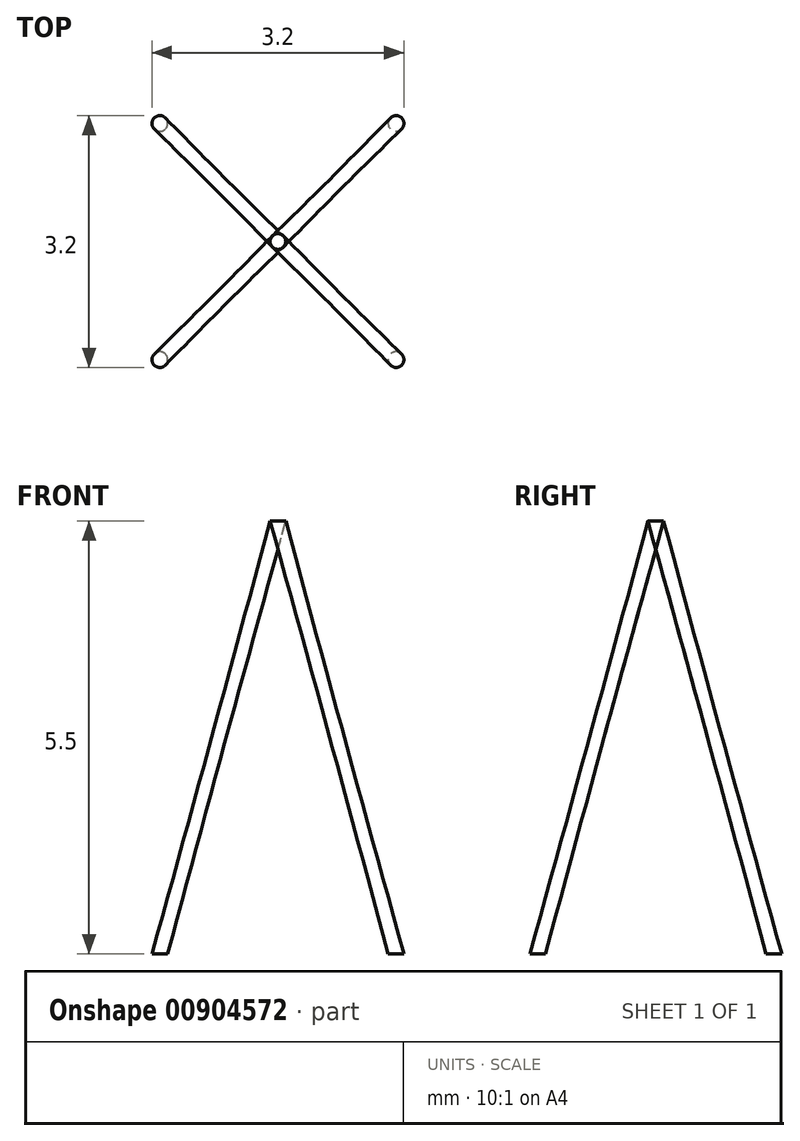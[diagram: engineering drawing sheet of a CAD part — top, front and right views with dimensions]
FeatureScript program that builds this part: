
annotation { "Feature Type Name" : "Feature", "Feature Type Description" : "" }
export const myFeature = defineFeature(function(context is Context, id is Id, definition is map)
    precondition{}
    {
        {
            var Q0;
            Q0=qCreatedBy(makeId("Top.planeOp"),FACE);
            var sketch = newSketch(context, id + "F0", { "sketchPlane" : qUnion([Q0])});
            skCircle(sketch, "E0", {"center": v(0, 0) * mm, "radius": 5 * mm});
            skLineSegment(sketch, "E1.bottom", {"start": v(1.5, -1.5) * mm, "end": v(-1.5, -1.5) * mm, "construction": true});
            skLineSegment(sketch, "E1.top", {"start": v(1.5, 1.5) * mm, "end": v(-1.5, 1.5) * mm, "construction": true});
            skLineSegment(sketch, "E1.left", {"start": v(1.5, -1.5) * mm, "end": v(1.5, 1.5) * mm, "construction": true});
            skLineSegment(sketch, "E1.right", {"start": v(-1.5, -1.5) * mm, "end": v(-1.5, 1.5) * mm, "construction": true});
            skCircle(sketch, "E2", {"center": v(-1.5, -1.5) * mm, "radius": 0.1 * mm});
            skCircle(sketch, "E3", {"center": v(1.5, -1.5) * mm, "radius": 0.1 * mm});
            skCircle(sketch, "E4", {"center": v(1.5, 1.5) * mm, "radius": 0.1 * mm});
            skCircle(sketch, "E5", {"center": v(-1.5, 1.5) * mm, "radius": 0.1 * mm});
            skSolve(sketch);
        }
        {
            var Q0;
            Q0=makeQuery(id+"F0.imprint","IMPRINT",FACE,{"disambiguationData":[TD([[makeQuery(id+"F0.imprint","IMPRINT",EDGE,{"derivedFrom":sQuery(id+"F0.wireOp",EDGE,"E0")}),1.0]])]});
            cPlane(context, id + "F1", {"entities" : qUnion([Q0]), "cplaneType" : CPlaneType.OFFSET, "offset" : 5.5 * mm, "width" : 150 * mm, "height" : 150 * mm});
        }
        {
            var Q0;
            Q0=qCreatedBy(id+"F1.planeOp",FACE);
            var sketch = newSketch(context, id + "F2", { "sketchPlane" : qUnion([Q0])});
            skPoint(sketch, "E6", {"position": v(0, 0) * mm});
            skCircle(sketch, "E7", {"center": v(0, 0) * mm, "radius": 0.1 * mm});
            skCircle(sketch, "E8", {"center": v(0, 0) * mm, "radius": 0.5 * mm});
            skSolve(sketch);
        }
        {
            var Q0;
            Q0=makeQuery(id+"F2.imprint","IMPRINT",FACE,{"disambiguationData":[TD([[makeQuery(id+"F2.imprint","IMPRINT",EDGE,{"derivedFrom":sQuery(id+"F2.wireOp",EDGE,"E7")}),1.0]])]});
            var Q1;
            Q1=makeQuery(id+"F0.imprint","IMPRINT",FACE,{"disambiguationData":[TD([[makeQuery(id+"F0.imprint","IMPRINT",EDGE,{"derivedFrom":sQuery(id+"F0.wireOp",EDGE,"E5")}),1.0]])]});
            loft(context, id + "F3", {"sheetProfilesArray" : [{ "sheetProfileEntities" : qUnion([Q0]) }, { "sheetProfileEntities" : qUnion([Q1]) }]});
        }
        {
            var Q1;
            Q1=makeQuery(id+"F0.imprint","IMPRINT",FACE,{"disambiguationData":[TD([[makeQuery(id+"F0.imprint","IMPRINT",EDGE,{"derivedFrom":sQuery(id+"F0.wireOp",EDGE,"E4")}),1.0]])]});
            var Q2;
            Q2=makeQuery(id+"F2.imprint","IMPRINT",FACE,{"disambiguationData":[TD([[makeQuery(id+"F2.imprint","IMPRINT",EDGE,{"derivedFrom":sQuery(id+"F2.wireOp",EDGE,"E7")}),1.0]])]});
            loft(context, id + "F4", {"sheetProfilesArray" : [{ "sheetProfileEntities" : qUnion([Q1]) }, { "sheetProfileEntities" : qUnion([Q2]) }]});
        }
        {
            var Q0;
            Q0=makeQuery(id+"F2.imprint","IMPRINT",FACE,{"disambiguationData":[TD([[makeQuery(id+"F2.imprint","IMPRINT",EDGE,{"derivedFrom":sQuery(id+"F2.wireOp",EDGE,"E7")}),1.0]])]});
            var Q1;
            Q1=makeQuery(id+"F0.imprint","IMPRINT",FACE,{"disambiguationData":[TD([[makeQuery(id+"F0.imprint","IMPRINT",EDGE,{"derivedFrom":sQuery(id+"F0.wireOp",EDGE,"E2")}),1.0]])]});
            loft(context, id + "F5", {"sheetProfilesArray" : [{ "sheetProfileEntities" : qUnion([Q0]) }, { "sheetProfileEntities" : qUnion([Q1]) }]});
        }
        {
            var Q0;
            Q0=makeQuery(id+"F0.imprint","IMPRINT",FACE,{"disambiguationData":[TD([[makeQuery(id+"F0.imprint","IMPRINT",EDGE,{"derivedFrom":sQuery(id+"F0.wireOp",EDGE,"E3")}),1.0]])]});
            var Q1;
            Q1=makeQuery(id+"F2.imprint","IMPRINT",FACE,{"disambiguationData":[TD([[makeQuery(id+"F2.imprint","IMPRINT",EDGE,{"derivedFrom":sQuery(id+"F2.wireOp",EDGE,"E7")}),1.0]])]});
            loft(context, id + "F6", {"sheetProfilesArray" : [{ "sheetProfileEntities" : qUnion([Q0]) }, { "sheetProfileEntities" : qUnion([Q1]) }]});
        }
    });
